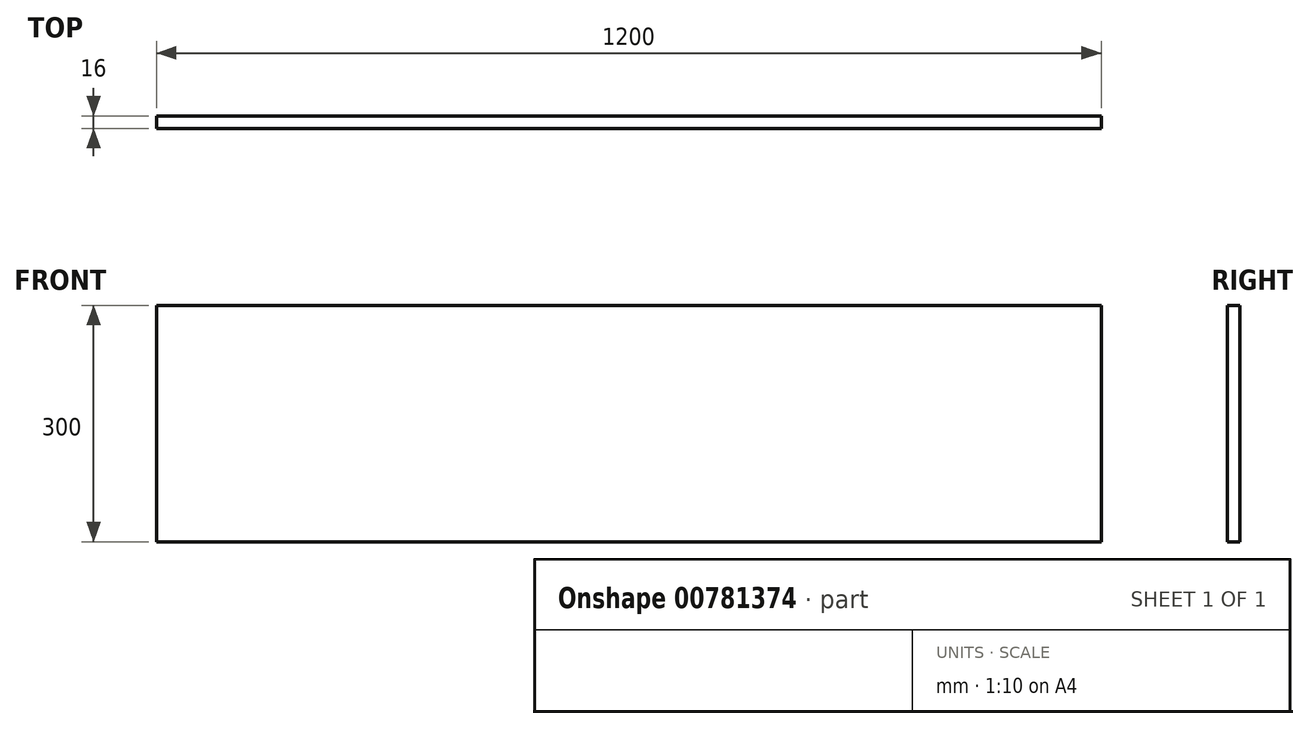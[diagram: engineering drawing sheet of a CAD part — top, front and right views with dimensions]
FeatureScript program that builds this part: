
annotation { "Feature Type Name" : "Feature", "Feature Type Description" : "" }
export const myFeature = defineFeature(function(context is Context, id is Id, definition is map)
    precondition{}
    {
        {
            var Q0;
            Q0=qCreatedBy(makeId("Front.planeOp"),FACE);
            var sketch = newSketch(context, id + "F0", { "sketchPlane" : qUnion([Q0])});
            skLineSegment(sketch, "E0.bottom", {"start": v(-600, -150) * mm, "end": v(600, -150) * mm});
            skLineSegment(sketch, "E0.top", {"start": v(-600, 150) * mm, "end": v(600, 150) * mm});
            skLineSegment(sketch, "E0.left", {"start": v(-600, -150) * mm, "end": v(-600, 150) * mm});
            skLineSegment(sketch, "E0.right", {"start": v(600, -150) * mm, "end": v(600, 150) * mm});
            skPoint(sketch, "E0.middle", {"position": v(0, 0) * mm});
            skSolve(sketch);
        }
        {
            var Q0;
            Q0=makeQuery(id+"F0.imprint","IMPRINT",FACE,{"disambiguationData":[TD([[makeQuery(id+"F0.imprint","IMPRINT",EDGE,{"derivedFrom":sQuery(id+"F0.wireOp",EDGE,"E0.bottom")}),1.0]])]});
            extrude(context, id + "F1", {"entities" : qUnion([Q0]), "depth" : 16 * mm, "offsetDistance" : 25 * mm});
        }
    });
